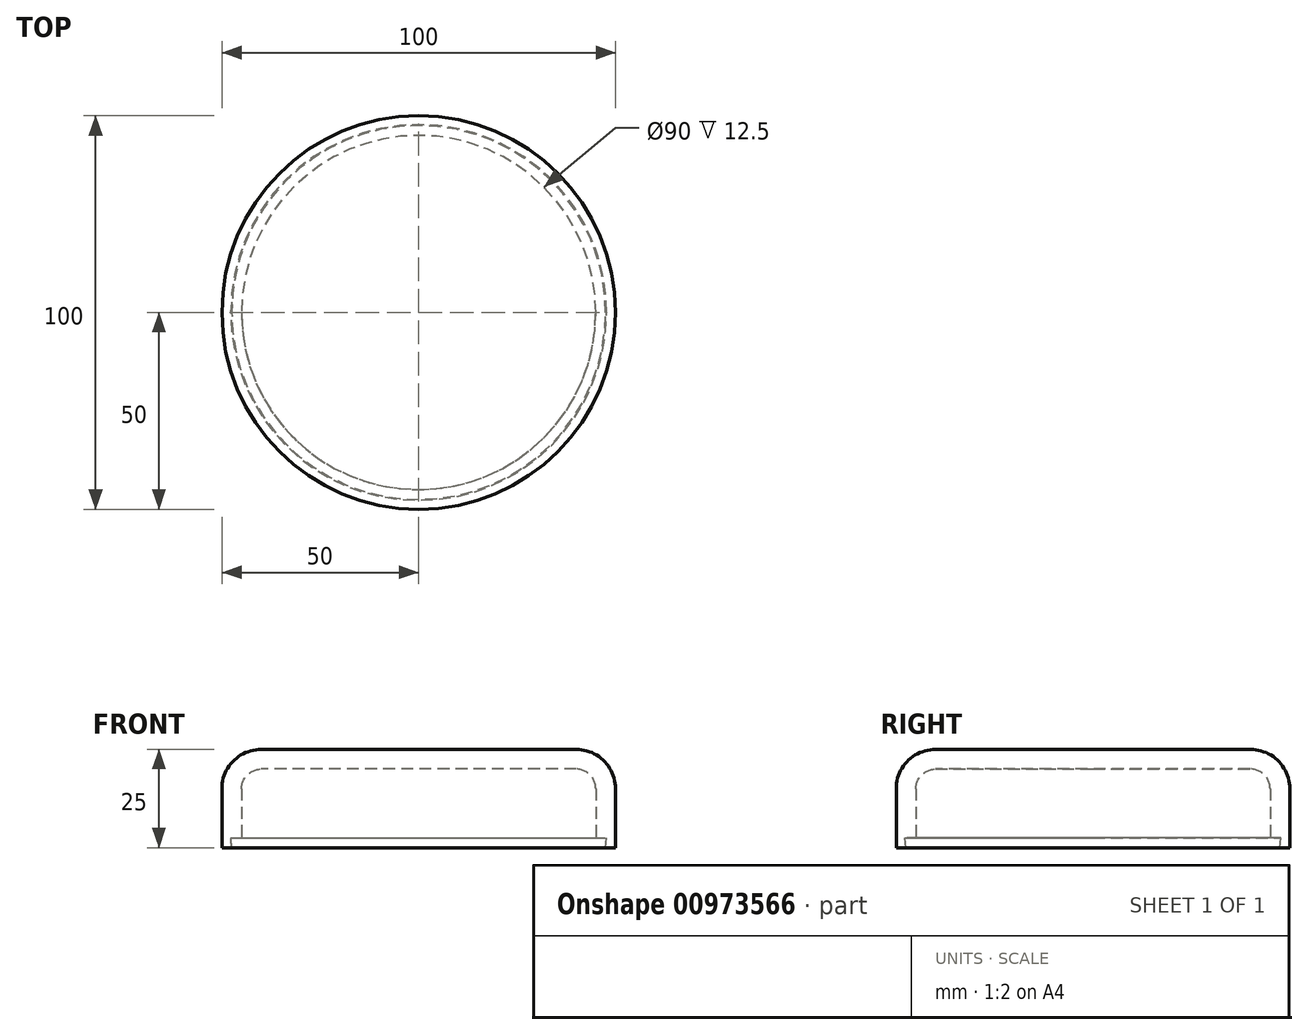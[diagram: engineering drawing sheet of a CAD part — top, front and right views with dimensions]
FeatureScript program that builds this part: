
annotation { "Feature Type Name" : "Feature", "Feature Type Description" : "" }
export const myFeature = defineFeature(function(context is Context, id is Id, definition is map)
    precondition{}
    {
        {
            var Q0;
            Q0=qCreatedBy(makeId("Top.planeOp"),FACE);
            var sketch = newSketch(context, id + "F0", { "sketchPlane" : qUnion([Q0])});
            skCircle(sketch, "E0", {"center": v(0, 0) * mm, "radius": 50 * mm});
            skSolve(sketch);
        }
        {
            var Q0;
            Q0=makeQuery(id+"F0.imprint","IMPRINT",FACE,{"disambiguationData":[TD([[makeQuery(id+"F0.imprint","IMPRINT",EDGE,{"derivedFrom":sQuery(id+"F0.wireOp",EDGE,"E0")}),1.0]])]});
            extrude(context, id + "F1", {"entities" : qUnion([Q0]), "depth" : 25 * mm, "offsetDistance" : 25 * mm});
        }
        {
            var Q0;
            Q0=makeQuery(id+"F1.opExtrude","CAP_EDGE",EDGE,{"disambiguationData":[OSD([sQuery(id+"F0.wireOp",EDGE,"E0")])],"isStart":false});
            fillet(context, id + "F2", {"entities" : qUnion([Q0]), "radius" : 10 * mm, "tangentPropagation" : true, "allowEdgeOverflow" : false});
        }
        {
            var Q0;
            Q0=makeQuery(id+"F1.opExtrude","CAP_FACE",FACE,{"disambiguationData":[OSD([sQuery(id+"F0.wireOp",EDGE,"E0")])],"isStart":true});
            shell(context, id + "F3", {"entities" : qUnion([Q0]), "thickness" : 5 * mm});
        }
        {
            var Q0;
            Q0=makeQuery(id+"F1.opExtrude","CAP_FACE",FACE,{"disambiguationData":[OSD([sQuery(id+"F0.wireOp",EDGE,"E0")])],"isStart":true});
            var sketch = newSketch(context, id + "F4", { "sketchPlane" : qUnion([Q0])});
            skCircle(sketch, "E1", {"center": v(0, 0) * mm, "radius": 47.5 * mm});
            skSolve(sketch);
        }
        {
            var Q0;
            Q0=makeQuery(id+"F4.imprint","IMPRINT",FACE,{"disambiguationData":[TD([[makeQuery(id+"F4.imprint","IMPRINT",EDGE,{"derivedFrom":sQuery(id+"F4.wireOp",EDGE,"E1")}),1.0]])]});
            extrude(context, id + "F5", {"entities" : qUnion([Q0]), "operationType" : NewBodyOperationType.REMOVE, "oppositeDirection" : true, "depth" : 2.5 * mm, "offsetDistance" : 25 * mm, "hasDraft" : true, "draftAngle" : 5 * degree});
        }
    });
